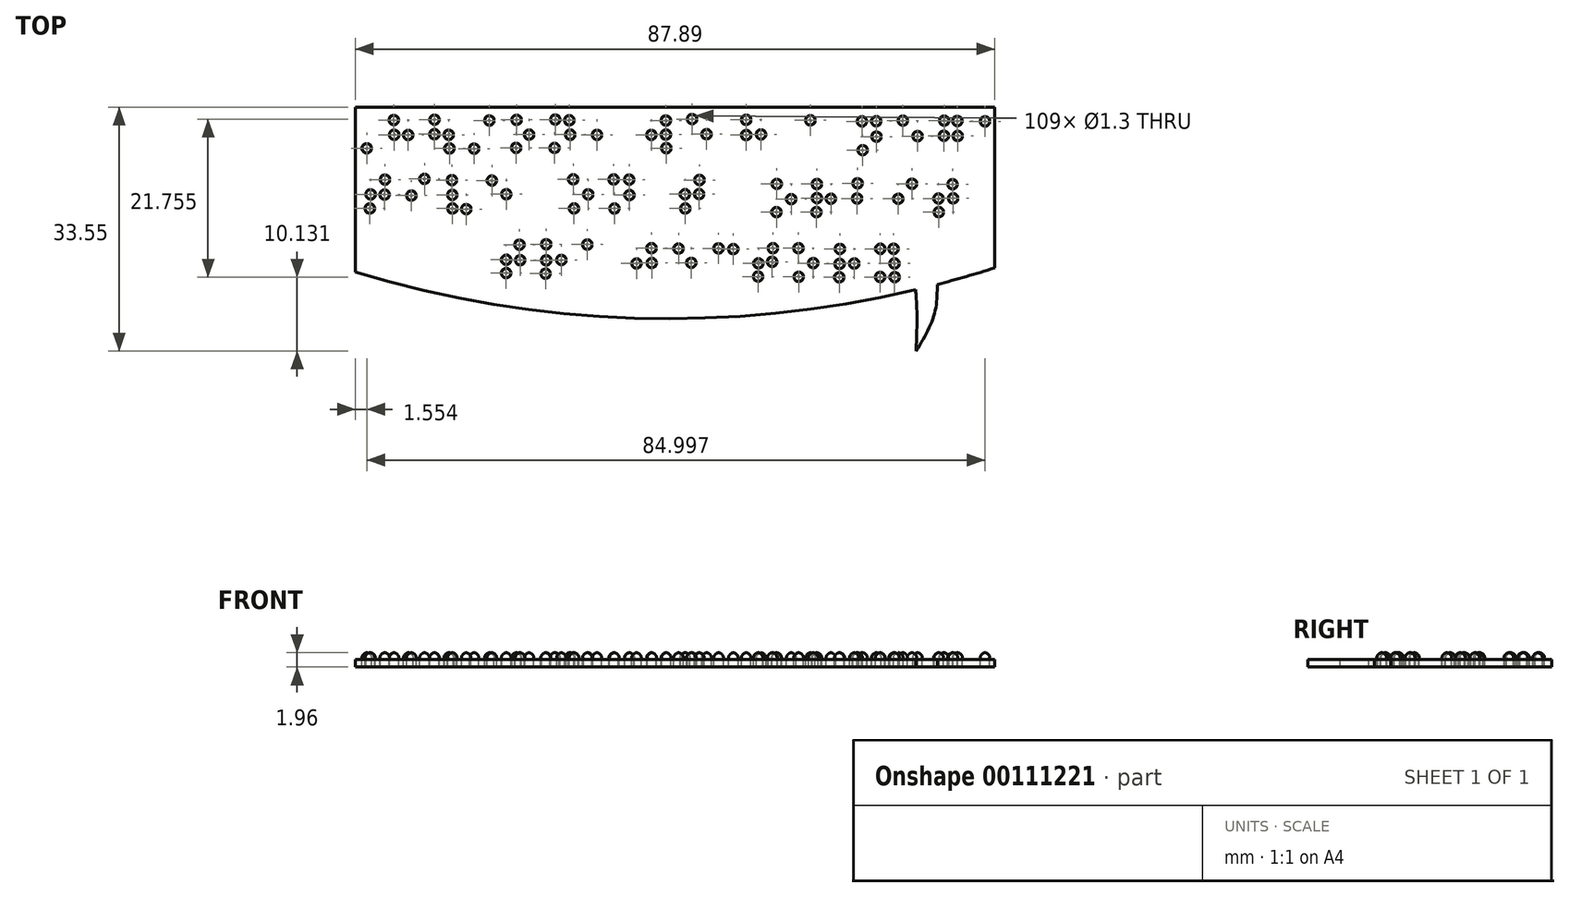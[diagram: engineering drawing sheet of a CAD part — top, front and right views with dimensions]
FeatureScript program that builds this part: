
annotation { "Feature Type Name" : "Feature", "Feature Type Description" : "" }
export const myFeature = defineFeature(function(context is Context, id is Id, definition is map)
    precondition{}
    {
        {
            var Q0;
            Q0=qCreatedBy(makeId("Top.planeOp"),FACE);
            var sketch = newSketch(context, id + "F0", { "sketchPlane" : qUnion([Q0])});
            skCircle(sketch, "E0", {"center": v(-65.84, 32.23) * mm, "radius": 0.65 * mm});
            skSolve(sketch);
        }
        {
            var Q0;
            Q0=qCreatedBy(makeId("Top.planeOp"),FACE);
            var sketch = newSketch(context, id + "F1", { "sketchPlane" : qUnion([Q0])});
            skCircle(sketch, "E1", {"center": v(-52.47, 59.18) * mm, "radius": 0.65 * mm});
            skCircle(sketch, "E2", {"center": v(-52.44, 57.14) * mm, "radius": 0.65 * mm});
            skCircle(sketch, "E3", {"center": v(-50.5, 57.1) * mm, "radius": 0.65 * mm});
            skCircle(sketch, "E4", {"center": v(-56.2, 55.29) * mm, "radius": 0.65 * mm});
            skCircle(sketch, "E5", {"center": v(-46.91, 57.22) * mm, "radius": 0.65 * mm});
            skCircle(sketch, "E6", {"center": v(-46.88, 59.22) * mm, "radius": 0.65 * mm});
            skCircle(sketch, "E7", {"center": v(-44.94, 57.14) * mm, "radius": 0.65 * mm});
            skCircle(sketch, "E8", {"center": v(-44.83, 55.27) * mm, "radius": 0.65 * mm});
            skCircle(sketch, "E9", {"center": v(-41.44, 55.24) * mm, "radius": 0.65 * mm});
            skCircle(sketch, "E10", {"center": v(-39.34, 59.11) * mm, "radius": 0.65 * mm});
            skCircle(sketch, "E11", {"center": v(-35.62, 59.2) * mm, "radius": 0.65 * mm});
            skCircle(sketch, "E12", {"center": v(-33.9, 57.16) * mm, "radius": 0.65 * mm});
            skCircle(sketch, "E13", {"center": v(-35.67, 55.34) * mm, "radius": 0.65 * mm});
            skCircle(sketch, "E14", {"center": v(-30.29, 59.23) * mm, "radius": 0.65 * mm});
            skCircle(sketch, "E15", {"center": v(-28.35, 59.14) * mm, "radius": 0.65 * mm});
            skCircle(sketch, "E16", {"center": v(-28.23, 57.15) * mm, "radius": 0.65 * mm});
            skCircle(sketch, "E17", {"center": v(-30.38, 55.34) * mm, "radius": 0.65 * mm});
            skCircle(sketch, "E18", {"center": v(-24.55, 57.13) * mm, "radius": 0.65 * mm});
            skCircle(sketch, "E19", {"center": v(-17.08, 57.12) * mm, "radius": 0.65 * mm});
            skCircle(sketch, "E20", {"center": v(-15.07, 57.17) * mm, "radius": 0.65 * mm});
            skCircle(sketch, "E21", {"center": v(-15.07, 59.1) * mm, "radius": 0.65 * mm});
            skCircle(sketch, "E22", {"center": v(-15.03, 55.3) * mm, "radius": 0.65 * mm});
            skCircle(sketch, "E23", {"center": v(-11.49, 59.3) * mm, "radius": 0.65 * mm});
            skCircle(sketch, "E24", {"center": v(-9.48, 57.22) * mm, "radius": 0.65 * mm});
            skCircle(sketch, "E25", {"center": v(-4.05, 59.2) * mm, "radius": 0.65 * mm});
            skCircle(sketch, "E26", {"center": v(-4.05, 57.1) * mm, "radius": 0.65 * mm});
            skCircle(sketch, "E27", {"center": v(-2, 57.2) * mm, "radius": 0.65 * mm});
            skCircle(sketch, "E28", {"center": v(4.77, 59.14) * mm, "radius": 0.65 * mm});
            skCircle(sketch, "E29", {"center": v(11.88, 59) * mm, "radius": 0.65 * mm});
            skCircle(sketch, "E30", {"center": v(13.83, 59.02) * mm, "radius": 0.65 * mm});
            skCircle(sketch, "E31", {"center": v(13.86, 56.89) * mm, "radius": 0.65 * mm});
            skCircle(sketch, "E32", {"center": v(11.97, 55.03) * mm, "radius": 0.65 * mm});
            skCircle(sketch, "E33", {"center": v(17.49, 59.09) * mm, "radius": 0.65 * mm});
            skCircle(sketch, "E34", {"center": v(19.52, 56.96) * mm, "radius": 0.65 * mm});
            skCircle(sketch, "E35", {"center": v(23.18, 59.09) * mm, "radius": 0.65 * mm});
            skCircle(sketch, "E36", {"center": v(23.13, 57) * mm, "radius": 0.65 * mm});
            skCircle(sketch, "E37", {"center": v(25.04, 56.98) * mm, "radius": 0.65 * mm});
            skCircle(sketch, "E38", {"center": v(25, 59.04) * mm, "radius": 0.65 * mm});
            skCircle(sketch, "E39", {"center": v(28.8, 58.99) * mm, "radius": 0.65 * mm});
            skCircle(sketch, "E40", {"center": v(-55.68, 48.95) * mm, "radius": 0.65 * mm});
            skCircle(sketch, "E41", {"center": v(-55.77, 47.01) * mm, "radius": 0.65 * mm});
            skCircle(sketch, "E42", {"center": v(-53.74, 48.92) * mm, "radius": 0.65 * mm});
            skCircle(sketch, "E43", {"center": v(-53.7, 50.98) * mm, "radius": 0.65 * mm});
            skCircle(sketch, "E44", {"center": v(-50.06, 48.78) * mm, "radius": 0.65 * mm});
            skCircle(sketch, "E45", {"center": v(-48.27, 51.07) * mm, "radius": 0.65 * mm});
            skCircle(sketch, "E46", {"center": v(-44.5, 50.9) * mm, "radius": 0.65 * mm});
            skCircle(sketch, "E47", {"center": v(-44.45, 48.87) * mm, "radius": 0.65 * mm});
            skCircle(sketch, "E48", {"center": v(-44.43, 47) * mm, "radius": 0.65 * mm});
            skCircle(sketch, "E49", {"center": v(-42.54, 46.91) * mm, "radius": 0.65 * mm});
            skCircle(sketch, "E50", {"center": v(-39, 50.85) * mm, "radius": 0.65 * mm});
            skCircle(sketch, "E51", {"center": v(-37.02, 48.97) * mm, "radius": 0.65 * mm});
            skCircle(sketch, "E52", {"center": v(-27.82, 51.02) * mm, "radius": 0.65 * mm});
            skCircle(sketch, "E53", {"center": v(-25.77, 48.94) * mm, "radius": 0.65 * mm});
            skCircle(sketch, "E54", {"center": v(-27.7, 47) * mm, "radius": 0.65 * mm});
            skCircle(sketch, "E55", {"center": v(-22.25, 51) * mm, "radius": 0.65 * mm});
            skCircle(sketch, "E56", {"center": v(-20.13, 50.97) * mm, "radius": 0.65 * mm});
            skCircle(sketch, "E57", {"center": v(-20.08, 48.84) * mm, "radius": 0.65 * mm});
            skCircle(sketch, "E58", {"center": v(-22.16, 47) * mm, "radius": 0.65 * mm});
            skCircle(sketch, "E59", {"center": v(-12.46, 48.96) * mm, "radius": 0.65 * mm});
            skCircle(sketch, "E60", {"center": v(-12.41, 47) * mm, "radius": 0.65 * mm});
            skCircle(sketch, "E61", {"center": v(-10.52, 48.99) * mm, "radius": 0.65 * mm});
            skCircle(sketch, "E62", {"center": v(-10.47, 50.93) * mm, "radius": 0.65 * mm});
            skCircle(sketch, "E63", {"center": v(0.16, 50.39) * mm, "radius": 0.65 * mm});
            skCircle(sketch, "E64", {"center": v(2.15, 48.3) * mm, "radius": 0.65 * mm});
            skCircle(sketch, "E65", {"center": v(0.12, 46.5) * mm, "radius": 0.65 * mm});
            skCircle(sketch, "E66", {"center": v(5.67, 50.36) * mm, "radius": 0.65 * mm});
            skCircle(sketch, "E67", {"center": v(5.69, 48.42) * mm, "radius": 0.65 * mm});
            skCircle(sketch, "E68", {"center": v(5.62, 46.5) * mm, "radius": 0.65 * mm});
            skCircle(sketch, "E69", {"center": v(7.6, 48.33) * mm, "radius": 0.65 * mm});
            skCircle(sketch, "E70", {"center": v(11.28, 50.48) * mm, "radius": 0.65 * mm});
            skCircle(sketch, "E71", {"center": v(11.2, 48.38) * mm, "radius": 0.65 * mm});
            skCircle(sketch, "E72", {"center": v(16.87, 48.33) * mm, "radius": 0.65 * mm});
            skCircle(sketch, "E73", {"center": v(18.75, 50.4) * mm, "radius": 0.65 * mm});
            skCircle(sketch, "E74", {"center": v(22.4, 48.38) * mm, "radius": 0.65 * mm});
            skCircle(sketch, "E75", {"center": v(24.32, 50.34) * mm, "radius": 0.65 * mm});
            skCircle(sketch, "E76", {"center": v(24.4, 48.4) * mm, "radius": 0.65 * mm});
            skCircle(sketch, "E77", {"center": v(22.44, 46.5) * mm, "radius": 0.65 * mm});
            skCircle(sketch, "E78", {"center": v(-37.03, 38.12) * mm, "radius": 0.65 * mm});
            skCircle(sketch, "E79", {"center": v(-37.03, 39.95) * mm, "radius": 0.65 * mm});
            skCircle(sketch, "E80", {"center": v(-35.12, 39.9) * mm, "radius": 0.65 * mm});
            skCircle(sketch, "E81", {"center": v(-35.2, 42.02) * mm, "radius": 0.65 * mm});
            skCircle(sketch, "E82", {"center": v(-31.53, 42.09) * mm, "radius": 0.65 * mm});
            skCircle(sketch, "E83", {"center": v(-31.53, 39.88) * mm, "radius": 0.65 * mm});
            skCircle(sketch, "E84", {"center": v(-31.62, 38.05) * mm, "radius": 0.65 * mm});
            skCircle(sketch, "E85", {"center": v(-29.46, 39.92) * mm, "radius": 0.65 * mm});
            skCircle(sketch, "E86", {"center": v(-25.9, 42.04) * mm, "radius": 0.65 * mm});
            skCircle(sketch, "E87", {"center": v(-19.12, 39.44) * mm, "radius": 0.65 * mm});
            skCircle(sketch, "E88", {"center": v(-17.02, 39.5) * mm, "radius": 0.65 * mm});
            skCircle(sketch, "E89", {"center": v(-17.07, 41.55) * mm, "radius": 0.65 * mm});
            skCircle(sketch, "E90", {"center": v(-13.34, 41.5) * mm, "radius": 0.65 * mm});
            skCircle(sketch, "E91", {"center": v(-11.59, 39.53) * mm, "radius": 0.65 * mm});
            skCircle(sketch, "E92", {"center": v(-7.83, 41.53) * mm, "radius": 0.65 * mm});
            skCircle(sketch, "E93", {"center": v(-5.8, 41.43) * mm, "radius": 0.65 * mm});
            skCircle(sketch, "E94", {"center": v(-2.36, 39.46) * mm, "radius": 0.65 * mm});
            skCircle(sketch, "E95", {"center": v(-2.41, 37.64) * mm, "radius": 0.65 * mm});
            skCircle(sketch, "E96", {"center": v(-0.47, 39.67) * mm, "radius": 0.65 * mm});
            skCircle(sketch, "E97", {"center": v(-0.38, 41.55) * mm, "radius": 0.65 * mm});
            skCircle(sketch, "E98", {"center": v(3.16, 41.54) * mm, "radius": 0.65 * mm});
            skCircle(sketch, "E99", {"center": v(5.18, 39.5) * mm, "radius": 0.65 * mm});
            skCircle(sketch, "E100", {"center": v(3.17, 37.61) * mm, "radius": 0.65 * mm});
            skCircle(sketch, "E101", {"center": v(8.83, 41.44) * mm, "radius": 0.65 * mm});
            skCircle(sketch, "E102", {"center": v(8.8, 39.39) * mm, "radius": 0.65 * mm});
            skCircle(sketch, "E103", {"center": v(8.75, 37.54) * mm, "radius": 0.65 * mm});
            skCircle(sketch, "E104", {"center": v(10.8, 39.44) * mm, "radius": 0.65 * mm});
            skCircle(sketch, "E105", {"center": v(14.4, 41.46) * mm, "radius": 0.65 * mm});
            skCircle(sketch, "E106", {"center": v(16.22, 41.46) * mm, "radius": 0.65 * mm});
            skCircle(sketch, "E107", {"center": v(16.35, 39.44) * mm, "radius": 0.65 * mm});
            skCircle(sketch, "E108", {"center": v(16.37, 37.57) * mm, "radius": 0.65 * mm});
            skCircle(sketch, "E109", {"center": v(14.37, 37.6) * mm, "radius": 0.65 * mm});
            skLineSegment(sketch, "E110", {"start": v(-57.76, 60.96) * mm, "end": v(30.13, 60.96) * mm});
            skLineSegment(sketch, "E111", {"start": v(30.13, 60.96) * mm, "end": v(30.13, 38.84) * mm});
            skLineSegment(sketch, "E112", {"start": v(-57.76, 60.96) * mm, "end": v(-57.76, 38.27) * mm});
            skArc(sketch, "E113", {"start": v(-57.76, 38.27) * mm, "mid": v(-13.77, 31.86) * mm, "end": v(30.13, 38.84) * mm});
            skFitSpline(sketch, "E114", {"points": [v(22.22, 36.56) * mm, v(21.77, 32.26) * mm, v(19.31, 27.41) * mm], "startDerivative": vector(-0.02, -9.29) * mm, "endDerivative": vector(-5.65, -9.2) * mm});
            skFitSpline(sketch, "E115", {"points": [v(19.25, 35.82) * mm, v(19.43, 32.38) * mm, v(19.31, 27.41) * mm], "startDerivative": vector(0.57, -7.27) * mm, "endDerivative": vector(-0.39, -9.52) * mm});
            skSolve(sketch);
        }
        {
            var Q0;
            Q0=qCreatedBy(makeId("Top.planeOp"),FACE);
            var sketch = newSketch(context, id + "F2", { "sketchPlane" : qUnion([Q0])});
            skLineSegment(sketch, "E116.bottom", {"start": v(-59.53, 60.83) * mm, "end": v(15.65, 60.83) * mm});
            skLineSegment(sketch, "E116.top", {"start": v(-59.53, 26.54) * mm, "end": v(15.65, 26.54) * mm});
            skLineSegment(sketch, "E116.left", {"start": v(-59.53, 60.83) * mm, "end": v(-59.53, 26.54) * mm});
            skLineSegment(sketch, "E116.right", {"start": v(15.65, 60.83) * mm, "end": v(15.65, 26.54) * mm});
            skLineSegment(sketch, "E117.bottom", {"start": v(15.65, 26.54) * mm, "end": v(-12.7, 26.54) * mm});
            skLineSegment(sketch, "E117.top", {"start": v(15.65, 45.59) * mm, "end": v(-12.7, 45.59) * mm});
            skLineSegment(sketch, "E117.left", {"start": v(15.65, 26.54) * mm, "end": v(15.65, 45.59) * mm});
            skLineSegment(sketch, "E117.right", {"start": v(-12.7, 26.54) * mm, "end": v(-12.7, 45.59) * mm});
            skSolve(sketch);
        }
        {
            var Q0;
            Q0=makeQuery(id+"F1.imprint","IMPRINT",FACE,{"disambiguationData":[TD([[makeQuery(id+"F1.imprint","IMPRINT",EDGE,{"derivedFrom":sQuery(id+"F1.wireOp",EDGE,"E81")}),1.0]])]});
            var Q1;
            Q1=makeQuery(id+"F1.imprint","IMPRINT",FACE,{"disambiguationData":[TD([[makeQuery(id+"F1.imprint","IMPRINT",EDGE,{"derivedFrom":sQuery(id+"F1.wireOp",EDGE,"E97")}),1.0]])]});
            var Q2;
            Q2=makeQuery(id+"F1.imprint","IMPRINT",FACE,{"disambiguationData":[TD([[makeQuery(id+"F1.imprint","IMPRINT",EDGE,{"derivedFrom":sQuery(id+"F1.wireOp",EDGE,"E27")}),1.0]])]});
            var Q3;
            Q3=makeQuery(id+"F0.imprint","IMPRINT",FACE,{"disambiguationData":[TD([[makeQuery(id+"F0.imprint","IMPRINT",EDGE,{"derivedFrom":sQuery(id+"F0.wireOp",EDGE,"E0")}),1.0]])]});
            var Q4;
            Q4=makeQuery(id+"F1.imprint","IMPRINT",FACE,{"disambiguationData":[TD([[makeQuery(id+"F1.imprint","IMPRINT",EDGE,{"derivedFrom":sQuery(id+"F1.wireOp",EDGE,"E43")}),1.0]])]});
            var Q5;
            Q5=makeQuery(id+"F1.imprint","IMPRINT",FACE,{"disambiguationData":[TD([[makeQuery(id+"F1.imprint","IMPRINT",EDGE,{"derivedFrom":sQuery(id+"F1.wireOp",EDGE,"E84")}),1.0]])]});
            var Q6;
            Q6=makeQuery(id+"F1.imprint","IMPRINT",FACE,{"disambiguationData":[TD([[makeQuery(id+"F1.imprint","IMPRINT",EDGE,{"derivedFrom":sQuery(id+"F1.wireOp",EDGE,"E100")}),1.0]])]});
            var Q7;
            Q7=makeQuery(id+"F1.imprint","IMPRINT",FACE,{"disambiguationData":[TD([[makeQuery(id+"F1.imprint","IMPRINT",EDGE,{"derivedFrom":sQuery(id+"F1.wireOp",EDGE,"E20")}),1.0]])]});
            var Q8;
            Q8=makeQuery(id+"F1.imprint","IMPRINT",FACE,{"disambiguationData":[TD([[makeQuery(id+"F1.imprint","IMPRINT",EDGE,{"derivedFrom":sQuery(id+"F1.wireOp",EDGE,"E36")}),1.0]])]});
            var Q9;
            Q9=makeQuery(id+"F1.imprint","IMPRINT",FACE,{"disambiguationData":[TD([[makeQuery(id+"F1.imprint","IMPRINT",EDGE,{"derivedFrom":sQuery(id+"F1.wireOp",EDGE,"E58")}),1.0]])]});
            var Q10;
            Q10=makeQuery(id+"F1.imprint","IMPRINT",FACE,{"disambiguationData":[TD([[makeQuery(id+"F1.imprint","IMPRINT",EDGE,{"derivedFrom":sQuery(id+"F1.wireOp",EDGE,"E52")}),1.0]])]});
            var Q11;
            Q11=makeQuery(id+"F1.imprint","IMPRINT",FACE,{"disambiguationData":[TD([[makeQuery(id+"F1.imprint","IMPRINT",EDGE,{"derivedFrom":sQuery(id+"F1.wireOp",EDGE,"E32")}),1.0]])]});
            var Q12;
            Q12=makeQuery(id+"F1.imprint","IMPRINT",FACE,{"disambiguationData":[TD([[makeQuery(id+"F1.imprint","IMPRINT",EDGE,{"derivedFrom":sQuery(id+"F1.wireOp",EDGE,"E74")}),1.0]])]});
            var Q13;
            Q13=makeQuery(id+"F1.imprint","IMPRINT",FACE,{"disambiguationData":[TD([[makeQuery(id+"F1.imprint","IMPRINT",EDGE,{"derivedFrom":sQuery(id+"F1.wireOp",EDGE,"E48")}),1.0]])]});
            var Q14;
            Q14=makeQuery(id+"F1.imprint","IMPRINT",FACE,{"disambiguationData":[TD([[makeQuery(id+"F1.imprint","IMPRINT",EDGE,{"derivedFrom":sQuery(id+"F1.wireOp",EDGE,"E90")}),1.0]])]});
            var Q15;
            Q15=makeQuery(id+"F1.imprint","IMPRINT",FACE,{"disambiguationData":[TD([[makeQuery(id+"F1.imprint","IMPRINT",EDGE,{"derivedFrom":sQuery(id+"F1.wireOp",EDGE,"E64")}),1.0]])]});
            var Q16;
            Q16=makeQuery(id+"F1.imprint","IMPRINT",FACE,{"disambiguationData":[TD([[makeQuery(id+"F1.imprint","IMPRINT",EDGE,{"derivedFrom":sQuery(id+"F1.wireOp",EDGE,"E80")}),1.0]])]});
            var Q17;
            Q17=makeQuery(id+"F1.imprint","IMPRINT",FACE,{"disambiguationData":[TD([[makeQuery(id+"F1.imprint","IMPRINT",EDGE,{"derivedFrom":sQuery(id+"F1.wireOp",EDGE,"E106")}),1.0]])]});
            var Q18;
            Q18=makeQuery(id+"F1.imprint","IMPRINT",FACE,{"disambiguationData":[TD([[makeQuery(id+"F1.imprint","IMPRINT",EDGE,{"derivedFrom":sQuery(id+"F1.wireOp",EDGE,"E26")}),1.0]])]});
            var Q19;
            Q19=makeQuery(id+"F1.imprint","IMPRINT",FACE,{"disambiguationData":[TD([[makeQuery(id+"F1.imprint","IMPRINT",EDGE,{"derivedFrom":sQuery(id+"F1.wireOp",EDGE,"E42")}),1.0]])]});
            var Q20;
            Q20=makeQuery(id+"F1.imprint","IMPRINT",FACE,{"disambiguationData":[TD([[makeQuery(id+"F1.imprint","IMPRINT",EDGE,{"derivedFrom":sQuery(id+"F1.wireOp",EDGE,"E83")}),1.0]])]});
            var Q21;
            Q21=makeQuery(id+"F1.imprint","IMPRINT",FACE,{"disambiguationData":[TD([[makeQuery(id+"F1.imprint","IMPRINT",EDGE,{"derivedFrom":sQuery(id+"F1.wireOp",EDGE,"E99")}),1.0]])]});
            var Q22;
            Q22=makeQuery(id+"F1.imprint","IMPRINT",FACE,{"disambiguationData":[TD([[makeQuery(id+"F1.imprint","IMPRINT",EDGE,{"derivedFrom":sQuery(id+"F1.wireOp",EDGE,"E17")}),1.0]])]});
            var Q23;
            Q23=makeQuery(id+"F1.imprint","IMPRINT",FACE,{"disambiguationData":[TD([[makeQuery(id+"F1.imprint","IMPRINT",EDGE,{"derivedFrom":sQuery(id+"F1.wireOp",EDGE,"E33")}),1.0]])]});
            var Q24;
            Q24=makeQuery(id+"F1.imprint","IMPRINT",FACE,{"disambiguationData":[TD([[makeQuery(id+"F1.imprint","IMPRINT",EDGE,{"derivedFrom":sQuery(id+"F1.wireOp",EDGE,"E23")}),1.0]])]});
            var Q25;
            Q25=makeQuery(id+"F1.imprint","IMPRINT",FACE,{"disambiguationData":[TD([[makeQuery(id+"F1.imprint","IMPRINT",EDGE,{"derivedFrom":sQuery(id+"F1.wireOp",EDGE,"E39")}),1.0]])]});
            var Q26;
            Q26=makeQuery(id+"F1.imprint","IMPRINT",FACE,{"disambiguationData":[TD([[makeQuery(id+"F1.imprint","IMPRINT",EDGE,{"derivedFrom":sQuery(id+"F1.wireOp",EDGE,"E55")}),1.0]])]});
            var Q27;
            Q27=makeQuery(id+"F1.imprint","IMPRINT",FACE,{"disambiguationData":[TD([[makeQuery(id+"F1.imprint","IMPRINT",EDGE,{"derivedFrom":sQuery(id+"F1.wireOp",EDGE,"E71")}),1.0]])]});
            var Q28;
            Q28=makeQuery(id+"F1.imprint","IMPRINT",FACE,{"disambiguationData":[TD([[makeQuery(id+"F1.imprint","IMPRINT",EDGE,{"derivedFrom":sQuery(id+"F1.wireOp",EDGE,"E87")}),1.0]])]});
            var Q29;
            Q29=makeQuery(id+"F1.imprint","IMPRINT",FACE,{"disambiguationData":[TD([[makeQuery(id+"F1.imprint","IMPRINT",EDGE,{"derivedFrom":sQuery(id+"F1.wireOp",EDGE,"E49")}),1.0]])]});
            var Q30;
            Q30=makeQuery(id+"F1.imprint","IMPRINT",FACE,{"disambiguationData":[TD([[makeQuery(id+"F1.imprint","IMPRINT",EDGE,{"derivedFrom":sQuery(id+"F1.wireOp",EDGE,"E65")}),1.0]])]});
            var Q31;
            Q31=makeQuery(id+"F1.imprint","IMPRINT",FACE,{"disambiguationData":[TD([[makeQuery(id+"F1.imprint","IMPRINT",EDGE,{"derivedFrom":sQuery(id+"F1.wireOp",EDGE,"E19")}),1.0]])]});
            var Q32;
            Q32=makeQuery(id+"F1.imprint","IMPRINT",FACE,{"disambiguationData":[TD([[makeQuery(id+"F1.imprint","IMPRINT",EDGE,{"derivedFrom":sQuery(id+"F1.wireOp",EDGE,"E51")}),1.0]])]});
            var Q33;
            Q33=makeQuery(id+"F1.imprint","IMPRINT",FACE,{"disambiguationData":[TD([[makeQuery(id+"F1.imprint","IMPRINT",EDGE,{"derivedFrom":sQuery(id+"F1.wireOp",EDGE,"E57")}),1.0]])]});
            var Q34;
            Q34=makeQuery(id+"F1.imprint","IMPRINT",FACE,{"disambiguationData":[TD([[makeQuery(id+"F1.imprint","IMPRINT",EDGE,{"derivedFrom":sQuery(id+"F1.wireOp",EDGE,"E73")}),1.0]])]});
            var Q35;
            Q35=makeQuery(id+"F1.imprint","IMPRINT",FACE,{"disambiguationData":[TD([[makeQuery(id+"F1.imprint","IMPRINT",EDGE,{"derivedFrom":sQuery(id+"F1.wireOp",EDGE,"E89")}),1.0]])]});
            var Q36;
            Q36=makeQuery(id+"F1.imprint","IMPRINT",FACE,{"disambiguationData":[TD([[makeQuery(id+"F1.imprint","IMPRINT",EDGE,{"derivedFrom":sQuery(id+"F1.wireOp",EDGE,"E105")}),1.0]])]});
            var Q37;
            Q37=makeQuery(id+"F1.imprint","IMPRINT",FACE,{"disambiguationData":[TD([[makeQuery(id+"F1.imprint","IMPRINT",EDGE,{"derivedFrom":sQuery(id+"F1.wireOp",EDGE,"E61")}),1.0]])]});
            var Q38;
            Q38=makeQuery(id+"F1.imprint","IMPRINT",FACE,{"disambiguationData":[TD([[makeQuery(id+"F1.imprint","IMPRINT",EDGE,{"derivedFrom":sQuery(id+"F1.wireOp",EDGE,"E77")}),1.0]])]});
            var Q39;
            Q39=makeQuery(id+"F1.imprint","IMPRINT",FACE,{"disambiguationData":[TD([[makeQuery(id+"F1.imprint","IMPRINT",EDGE,{"derivedFrom":sQuery(id+"F1.wireOp",EDGE,"E13")}),1.0]])]});
            var Q40;
            Q40=makeQuery(id+"F1.imprint","IMPRINT",FACE,{"disambiguationData":[TD([[makeQuery(id+"F1.imprint","IMPRINT",EDGE,{"derivedFrom":sQuery(id+"F1.wireOp",EDGE,"E10")}),1.0]])]});
            var Q41;
            Q41=makeQuery(id+"F1.imprint","IMPRINT",FACE,{"disambiguationData":[TD([[makeQuery(id+"F1.imprint","IMPRINT",EDGE,{"derivedFrom":sQuery(id+"F1.wireOp",EDGE,"E12")}),1.0]])]});
            var Q42;
            Q42=makeQuery(id+"F1.imprint","IMPRINT",FACE,{"disambiguationData":[TD([[makeQuery(id+"F1.imprint","IMPRINT",EDGE,{"derivedFrom":sQuery(id+"F1.wireOp",EDGE,"E11")}),1.0]])]});
            var Q43;
            Q43=makeQuery(id+"F1.imprint","IMPRINT",FACE,{"disambiguationData":[TD([[makeQuery(id+"F1.imprint","IMPRINT",EDGE,{"derivedFrom":sQuery(id+"F1.wireOp",EDGE,"E25")}),1.0]])]});
            var Q44;
            Q44=makeQuery(id+"F1.imprint","IMPRINT",FACE,{"disambiguationData":[TD([[makeQuery(id+"F1.imprint","IMPRINT",EDGE,{"derivedFrom":sQuery(id+"F1.wireOp",EDGE,"E7")}),1.0]])]});
            var Q45;
            Q45=makeQuery(id+"F1.imprint","IMPRINT",FACE,{"disambiguationData":[TD([[makeQuery(id+"F1.imprint","IMPRINT",EDGE,{"derivedFrom":sQuery(id+"F1.wireOp",EDGE,"E8")}),1.0]])]});
            var Q46;
            Q46=makeQuery(id+"F1.imprint","IMPRINT",FACE,{"disambiguationData":[TD([[makeQuery(id+"F1.imprint","IMPRINT",EDGE,{"derivedFrom":sQuery(id+"F1.wireOp",EDGE,"E41")}),1.0]])]});
            var Q47;
            Q47=makeQuery(id+"F1.imprint","IMPRINT",FACE,{"disambiguationData":[TD([[makeQuery(id+"F1.imprint","IMPRINT",EDGE,{"derivedFrom":sQuery(id+"F1.wireOp",EDGE,"E82")}),1.0]])]});
            var Q48;
            Q48=makeQuery(id+"F1.imprint","IMPRINT",FACE,{"disambiguationData":[TD([[makeQuery(id+"F1.imprint","IMPRINT",EDGE,{"derivedFrom":sQuery(id+"F1.wireOp",EDGE,"E93")}),1.0]])]});
            var Q49;
            Q49=makeQuery(id+"F1.imprint","IMPRINT",FACE,{"disambiguationData":[TD([[makeQuery(id+"F1.imprint","IMPRINT",EDGE,{"derivedFrom":sQuery(id+"F1.wireOp",EDGE,"E98")}),1.0]])]});
            var Q50;
            Q50=makeQuery(id+"F1.imprint","IMPRINT",FACE,{"disambiguationData":[TD([[makeQuery(id+"F1.imprint","IMPRINT",EDGE,{"derivedFrom":sQuery(id+"F1.wireOp",EDGE,"E18")}),1.0]])]});
            var Q51;
            Q51=makeQuery(id+"F1.imprint","IMPRINT",FACE,{"disambiguationData":[TD([[makeQuery(id+"F1.imprint","IMPRINT",EDGE,{"derivedFrom":sQuery(id+"F1.wireOp",EDGE,"E34")}),1.0]])]});
            var Q52;
            Q52=makeQuery(id+"F1.imprint","IMPRINT",FACE,{"disambiguationData":[TD([[makeQuery(id+"F1.imprint","IMPRINT",EDGE,{"derivedFrom":sQuery(id+"F1.wireOp",EDGE,"E50")}),1.0]])]});
            var Q53;
            Q53=makeQuery(id+"F1.imprint","IMPRINT",FACE,{"disambiguationData":[TD([[makeQuery(id+"F1.imprint","IMPRINT",EDGE,{"derivedFrom":sQuery(id+"F1.wireOp",EDGE,"E45")}),1.0]])]});
            var Q54;
            Q54=makeQuery(id+"F1.imprint","IMPRINT",FACE,{"disambiguationData":[TD([[makeQuery(id+"F1.imprint","IMPRINT",EDGE,{"derivedFrom":sQuery(id+"F1.wireOp",EDGE,"E86")}),1.0]])]});
            var Q55;
            Q55=makeQuery(id+"F1.imprint","IMPRINT",FACE,{"disambiguationData":[TD([[makeQuery(id+"F1.imprint","IMPRINT",EDGE,{"derivedFrom":sQuery(id+"F1.wireOp",EDGE,"E79")}),1.0]])]});
            var Q56;
            Q56=makeQuery(id+"F1.imprint","IMPRINT",FACE,{"disambiguationData":[TD([[makeQuery(id+"F1.imprint","IMPRINT",EDGE,{"derivedFrom":sQuery(id+"F1.wireOp",EDGE,"E31")}),1.0]])]});
            var Q57;
            Q57=makeQuery(id+"F1.imprint","IMPRINT",FACE,{"disambiguationData":[TD([[makeQuery(id+"F1.imprint","IMPRINT",EDGE,{"derivedFrom":sQuery(id+"F1.wireOp",EDGE,"E22")}),1.0]])]});
            var Q58;
            Q58=makeQuery(id+"F1.imprint","IMPRINT",FACE,{"disambiguationData":[TD([[makeQuery(id+"F1.imprint","IMPRINT",EDGE,{"derivedFrom":sQuery(id+"F1.wireOp",EDGE,"E54")}),1.0]])]});
            var Q59;
            Q59=makeQuery(id+"F1.imprint","IMPRINT",FACE,{"disambiguationData":[TD([[makeQuery(id+"F1.imprint","IMPRINT",EDGE,{"derivedFrom":sQuery(id+"F1.wireOp",EDGE,"E6")}),1.0]])]});
            var Q60;
            Q60=makeQuery(id+"F1.imprint","IMPRINT",FACE,{"disambiguationData":[TD([[makeQuery(id+"F1.imprint","IMPRINT",EDGE,{"derivedFrom":sQuery(id+"F1.wireOp",EDGE,"E66")}),1.0]])]});
            var Q61;
            Q61=makeQuery(id+"F1.imprint","IMPRINT",FACE,{"disambiguationData":[TD([[makeQuery(id+"F1.imprint","IMPRINT",EDGE,{"derivedFrom":sQuery(id+"F1.wireOp",EDGE,"E5")}),1.0]])]});
            var Q62;
            Q62=makeQuery(id+"F1.imprint","IMPRINT",FACE,{"disambiguationData":[TD([[makeQuery(id+"F1.imprint","IMPRINT",EDGE,{"derivedFrom":sQuery(id+"F1.wireOp",EDGE,"E70")}),1.0]])]});
            var Q63;
            Q63=makeQuery(id+"F1.imprint","IMPRINT",FACE,{"disambiguationData":[TD([[makeQuery(id+"F1.imprint","IMPRINT",EDGE,{"derivedFrom":sQuery(id+"F1.wireOp",EDGE,"E47")}),1.0]])]});
            var Q64;
            Q64=makeQuery(id+"F1.imprint","IMPRINT",FACE,{"disambiguationData":[TD([[makeQuery(id+"F1.imprint","IMPRINT",EDGE,{"derivedFrom":sQuery(id+"F1.wireOp",EDGE,"E63")}),1.0]])]});
            var Q65;
            Q65=makeQuery(id+"F1.imprint","IMPRINT",FACE,{"disambiguationData":[TD([[makeQuery(id+"F1.imprint","IMPRINT",EDGE,{"derivedFrom":sQuery(id+"F1.wireOp",EDGE,"E4")}),1.0]])]});
            var Q66;
            Q66=makeQuery(id+"F1.imprint","IMPRINT",FACE,{"disambiguationData":[TD([[makeQuery(id+"F1.imprint","IMPRINT",EDGE,{"derivedFrom":sQuery(id+"F1.wireOp",EDGE,"E3")}),1.0]])]});
            var Q67;
            Q67=makeQuery(id+"F1.imprint","IMPRINT",FACE,{"disambiguationData":[TD([[makeQuery(id+"F1.imprint","IMPRINT",EDGE,{"derivedFrom":sQuery(id+"F1.wireOp",EDGE,"E2")}),1.0]])]});
            var Q68;
            Q68=makeQuery(id+"F1.imprint","IMPRINT",FACE,{"disambiguationData":[TD([[makeQuery(id+"F1.imprint","IMPRINT",EDGE,{"derivedFrom":sQuery(id+"F1.wireOp",EDGE,"E56")}),1.0]])]});
            var Q69;
            Q69=makeQuery(id+"F1.imprint","IMPRINT",FACE,{"disambiguationData":[TD([[makeQuery(id+"F1.imprint","IMPRINT",EDGE,{"derivedFrom":sQuery(id+"F1.wireOp",EDGE,"E72")}),1.0]])]});
            var Q70;
            Q70=makeQuery(id+"F1.imprint","IMPRINT",FACE,{"disambiguationData":[TD([[makeQuery(id+"F1.imprint","IMPRINT",EDGE,{"derivedFrom":sQuery(id+"F1.wireOp",EDGE,"E1")}),1.0]])]});
            var Q71;
            Q71=makeQuery(id+"F1.imprint","IMPRINT",FACE,{"disambiguationData":[TD([[makeQuery(id+"F1.imprint","IMPRINT",EDGE,{"derivedFrom":sQuery(id+"F1.wireOp",EDGE,"E88")}),1.0]])]});
            var Q72;
            Q72=makeQuery(id+"F1.imprint","IMPRINT",FACE,{"disambiguationData":[TD([[makeQuery(id+"F1.imprint","IMPRINT",EDGE,{"derivedFrom":sQuery(id+"F1.wireOp",EDGE,"E60")}),1.0]])]});
            var Q73;
            Q73=makeQuery(id+"F1.imprint","IMPRINT",FACE,{"disambiguationData":[TD([[makeQuery(id+"F1.imprint","IMPRINT",EDGE,{"derivedFrom":sQuery(id+"F1.wireOp",EDGE,"E76")}),1.0]])]});
            var Q74;
            Q74=makeQuery(id+"F1.imprint","IMPRINT",FACE,{"disambiguationData":[TD([[makeQuery(id+"F1.imprint","IMPRINT",EDGE,{"derivedFrom":sQuery(id+"F1.wireOp",EDGE,"E92")}),1.0]])]});
            var Q75;
            Q75=makeQuery(id+"F1.imprint","IMPRINT",FACE,{"disambiguationData":[TD([[makeQuery(id+"F1.imprint","IMPRINT",EDGE,{"derivedFrom":sQuery(id+"F1.wireOp",EDGE,"E15")}),1.0]])]});
            var Q76;
            Q76=makeQuery(id+"F1.imprint","IMPRINT",FACE,{"disambiguationData":[TD([[makeQuery(id+"F1.imprint","IMPRINT",EDGE,{"derivedFrom":sQuery(id+"F1.wireOp",EDGE,"E14")}),1.0]])]});
            var Q77;
            Q77=makeQuery(id+"F1.imprint","IMPRINT",FACE,{"disambiguationData":[TD([[makeQuery(id+"F1.imprint","IMPRINT",EDGE,{"derivedFrom":sQuery(id+"F1.wireOp",EDGE,"E44")}),1.0]])]});
            var Q78;
            Q78=makeQuery(id+"F1.imprint","IMPRINT",FACE,{"disambiguationData":[TD([[makeQuery(id+"F1.imprint","IMPRINT",EDGE,{"derivedFrom":sQuery(id+"F1.wireOp",EDGE,"E28")}),1.0]])]});
            var Q79;
            Q79=makeQuery(id+"F1.imprint","IMPRINT",FACE,{"disambiguationData":[TD([[makeQuery(id+"F1.imprint","IMPRINT",EDGE,{"derivedFrom":sQuery(id+"F1.wireOp",EDGE,"E78")}),1.0]])]});
            var Q80;
            Q80=makeQuery(id+"F1.imprint","IMPRINT",FACE,{"disambiguationData":[TD([[makeQuery(id+"F1.imprint","IMPRINT",EDGE,{"derivedFrom":sQuery(id+"F1.wireOp",EDGE,"E85")}),1.0]])]});
            var Q81;
            Q81=makeQuery(id+"F1.imprint","IMPRINT",FACE,{"disambiguationData":[TD([[makeQuery(id+"F1.imprint","IMPRINT",EDGE,{"derivedFrom":sQuery(id+"F1.wireOp",EDGE,"E16")}),1.0]])]});
            var Q82;
            Q82=makeQuery(id+"F1.imprint","IMPRINT",FACE,{"disambiguationData":[TD([[makeQuery(id+"F1.imprint","IMPRINT",EDGE,{"derivedFrom":sQuery(id+"F1.wireOp",EDGE,"E24")}),1.0]])]});
            var Q83;
            Q83=makeQuery(id+"F1.imprint","IMPRINT",FACE,{"disambiguationData":[TD([[makeQuery(id+"F1.imprint","IMPRINT",EDGE,{"derivedFrom":sQuery(id+"F1.wireOp",EDGE,"E40")}),1.0]])]});
            var Q84;
            Q84=makeQuery(id+"F1.imprint","IMPRINT",FACE,{"disambiguationData":[TD([[makeQuery(id+"F1.imprint","IMPRINT",EDGE,{"derivedFrom":sQuery(id+"F1.wireOp",EDGE,"E101")}),1.0]])]});
            var Q85;
            Q85=makeQuery(id+"F1.imprint","IMPRINT",FACE,{"disambiguationData":[TD([[makeQuery(id+"F1.imprint","IMPRINT",EDGE,{"derivedFrom":sQuery(id+"F1.wireOp",EDGE,"E21")}),1.0]])]});
            var Q86;
            Q86=makeQuery(id+"F1.imprint","IMPRINT",FACE,{"disambiguationData":[TD([[makeQuery(id+"F1.imprint","IMPRINT",EDGE,{"derivedFrom":sQuery(id+"F1.wireOp",EDGE,"E37")}),1.0]])]});
            var Q87;
            Q87=makeQuery(id+"F1.imprint","IMPRINT",FACE,{"disambiguationData":[TD([[makeQuery(id+"F1.imprint","IMPRINT",EDGE,{"derivedFrom":sQuery(id+"F1.wireOp",EDGE,"E46")}),1.0]])]});
            var Q88;
            Q88=makeQuery(id+"F1.imprint","IMPRINT",FACE,{"disambiguationData":[TD([[makeQuery(id+"F1.imprint","IMPRINT",EDGE,{"derivedFrom":sQuery(id+"F1.wireOp",EDGE,"E62")}),1.0]])]});
            var Q89;
            Q89=makeQuery(id+"F1.imprint","IMPRINT",FACE,{"disambiguationData":[TD([[makeQuery(id+"F1.imprint","IMPRINT",EDGE,{"derivedFrom":sQuery(id+"F1.wireOp",EDGE,"E59")}),1.0]])]});
            var Q90;
            Q90=makeQuery(id+"F1.imprint","IMPRINT",FACE,{"disambiguationData":[TD([[makeQuery(id+"F1.imprint","IMPRINT",EDGE,{"derivedFrom":sQuery(id+"F1.wireOp",EDGE,"E75")}),1.0]])]});
            var Q91;
            Q91=makeQuery(id+"F1.imprint","IMPRINT",FACE,{"disambiguationData":[TD([[makeQuery(id+"F1.imprint","IMPRINT",EDGE,{"derivedFrom":sQuery(id+"F1.wireOp",EDGE,"E91")}),1.0]])]});
            var Q92;
            Q92=makeQuery(id+"F1.imprint","IMPRINT",FACE,{"disambiguationData":[TD([[makeQuery(id+"F1.imprint","IMPRINT",EDGE,{"derivedFrom":sQuery(id+"F1.wireOp",EDGE,"E9")}),1.0]])]});
            var Q93;
            Q93=makeQuery(id+"F1.imprint","IMPRINT",FACE,{"disambiguationData":[TD([[makeQuery(id+"F1.imprint","IMPRINT",EDGE,{"derivedFrom":sQuery(id+"F1.wireOp",EDGE,"E96")}),1.0]])]});
            var Q94;
            Q94=makeQuery(id+"F1.imprint","IMPRINT",FACE,{"disambiguationData":[TD([[makeQuery(id+"F1.imprint","IMPRINT",EDGE,{"derivedFrom":sQuery(id+"F1.wireOp",EDGE,"E68")}),1.0]])]});
            var Q95;
            Q95=makeQuery(id+"F1.imprint","IMPRINT",FACE,{"disambiguationData":[TD([[makeQuery(id+"F1.imprint","IMPRINT",EDGE,{"derivedFrom":sQuery(id+"F1.wireOp",EDGE,"E35")}),1.0]])]});
            var Q96;
            Q96=makeQuery(id+"F1.imprint","IMPRINT",FACE,{"disambiguationData":[TD([[makeQuery(id+"F1.imprint","IMPRINT",EDGE,{"derivedFrom":sQuery(id+"F1.wireOp",EDGE,"E103")}),1.0]])]});
            var Q97;
            Q97=makeQuery(id+"F1.imprint","IMPRINT",FACE,{"disambiguationData":[TD([[makeQuery(id+"F1.imprint","IMPRINT",EDGE,{"derivedFrom":sQuery(id+"F1.wireOp",EDGE,"E67")}),1.0]])]});
            var Q98;
            Q98=makeQuery(id+"F1.imprint","IMPRINT",FACE,{"disambiguationData":[TD([[makeQuery(id+"F1.imprint","IMPRINT",EDGE,{"derivedFrom":sQuery(id+"F1.wireOp",EDGE,"E109")}),1.0]])]});
            var Q99;
            Q99=makeQuery(id+"F1.imprint","IMPRINT",FACE,{"disambiguationData":[TD([[makeQuery(id+"F1.imprint","IMPRINT",EDGE,{"derivedFrom":sQuery(id+"F1.wireOp",EDGE,"E29")}),1.0]])]});
            var Q100;
            Q100=makeQuery(id+"F1.imprint","IMPRINT",FACE,{"disambiguationData":[TD([[makeQuery(id+"F1.imprint","IMPRINT",EDGE,{"derivedFrom":sQuery(id+"F1.wireOp",EDGE,"E102")}),1.0]])]});
            var Q101;
            Q101=makeQuery(id+"F1.imprint","IMPRINT",FACE,{"disambiguationData":[TD([[makeQuery(id+"F1.imprint","IMPRINT",EDGE,{"derivedFrom":sQuery(id+"F1.wireOp",EDGE,"E95")}),1.0]])]});
            var Q102;
            Q102=makeQuery(id+"F1.imprint","IMPRINT",FACE,{"disambiguationData":[TD([[makeQuery(id+"F1.imprint","IMPRINT",EDGE,{"derivedFrom":sQuery(id+"F1.wireOp",EDGE,"E38")}),1.0]])]});
            var Q103;
            Q103=makeQuery(id+"F1.imprint","IMPRINT",FACE,{"disambiguationData":[TD([[makeQuery(id+"F1.imprint","IMPRINT",EDGE,{"derivedFrom":sQuery(id+"F1.wireOp",EDGE,"E108")}),1.0]])]});
            var Q104;
            Q104=makeQuery(id+"F1.imprint","IMPRINT",FACE,{"disambiguationData":[TD([[makeQuery(id+"F1.imprint","IMPRINT",EDGE,{"derivedFrom":sQuery(id+"F1.wireOp",EDGE,"E104")}),1.0]])]});
            var Q105;
            Q105=makeQuery(id+"F1.imprint","IMPRINT",FACE,{"disambiguationData":[TD([[makeQuery(id+"F1.imprint","IMPRINT",EDGE,{"derivedFrom":sQuery(id+"F1.wireOp",EDGE,"E94")}),1.0]])]});
            var Q106;
            Q106=makeQuery(id+"F1.imprint","IMPRINT",FACE,{"disambiguationData":[TD([[makeQuery(id+"F1.imprint","IMPRINT",EDGE,{"derivedFrom":sQuery(id+"F1.wireOp",EDGE,"E30")}),1.0]])]});
            var Q107;
            Q107=makeQuery(id+"F1.imprint","IMPRINT",FACE,{"disambiguationData":[TD([[makeQuery(id+"F1.imprint","IMPRINT",EDGE,{"derivedFrom":sQuery(id+"F1.wireOp",EDGE,"E53")}),1.0]])]});
            var Q108;
            Q108=makeQuery(id+"F1.imprint","IMPRINT",FACE,{"disambiguationData":[TD([[makeQuery(id+"F1.imprint","IMPRINT",EDGE,{"derivedFrom":sQuery(id+"F1.wireOp",EDGE,"E69")}),1.0]])]});
            var Q109;
            Q109=makeQuery(id+"F1.imprint","IMPRINT",FACE,{"disambiguationData":[TD([[makeQuery(id+"F1.imprint","IMPRINT",EDGE,{"derivedFrom":sQuery(id+"F1.wireOp",EDGE,"E107")}),1.0]])]});
            extrude(context, id + "F3", {"entities" : qUnion([Q0, Q1, Q2, Q3, Q4, Q5, Q6, Q7, Q8, Q9, Q10, Q11, Q12, Q13, Q14, Q15, Q16, Q17, Q18, Q19, Q20, Q21, Q22, Q23, Q24, Q25, Q26, Q27, Q28, Q29, Q30, Q31, Q32, Q33, Q34, Q35, Q36, Q37, Q38, Q39, Q40, Q41, Q42, Q43, Q44, Q45, Q46, Q47, Q48, Q49, Q50, Q51, Q52, Q53, Q54, Q55, Q56, Q57, Q58, Q59, Q60, Q61, Q62, Q63, Q64, Q65, Q66, Q67, Q68, Q69, Q70, Q71, Q72, Q73, Q74, Q75, Q76, Q77, Q78, Q79, Q80, Q81, Q82, Q83, Q84, Q85, Q86, Q87, Q88, Q89, Q90, Q91, Q92, Q93, Q94, Q95, Q96, Q97, Q98, Q99, Q100, Q101, Q102, Q103, Q104, Q105, Q106, Q107, Q108, Q109]), "depth" : 0.94 * mm});
        }
        {
            var Q0;
            Q0=makeQuery(id+"F3.opExtrude","CAP_EDGE",EDGE,{"disambiguationData":[OSD([sQuery(id+"F1.wireOp",EDGE,"E4")])],"isStart":false});
            var Q1;
            Q1=makeQuery(id+"F3.opExtrude","CAP_EDGE",EDGE,{"disambiguationData":[OSD([sQuery(id+"F1.wireOp",EDGE,"E2")])],"isStart":false});
            var Q2;
            Q2=makeQuery(id+"F3.opExtrude","CAP_EDGE",EDGE,{"disambiguationData":[OSD([sQuery(id+"F1.wireOp",EDGE,"E3")])],"isStart":false});
            var Q3;
            Q3=makeQuery(id+"F3.opExtrude","CAP_EDGE",EDGE,{"disambiguationData":[OSD([sQuery(id+"F1.wireOp",EDGE,"E5")])],"isStart":false});
            var Q4;
            Q4=makeQuery(id+"F3.opExtrude","CAP_EDGE",EDGE,{"disambiguationData":[OSD([sQuery(id+"F1.wireOp",EDGE,"E8")])],"isStart":false});
            var Q5;
            Q5=makeQuery(id+"F3.opExtrude","CAP_EDGE",EDGE,{"disambiguationData":[OSD([sQuery(id+"F1.wireOp",EDGE,"E9")])],"isStart":false});
            var Q6;
            Q6=makeQuery(id+"F3.opExtrude","CAP_EDGE",EDGE,{"disambiguationData":[OSD([sQuery(id+"F1.wireOp",EDGE,"E15")])],"isStart":false});
            var Q7;
            Q7=makeQuery(id+"F3.opExtrude","CAP_EDGE",EDGE,{"disambiguationData":[OSD([sQuery(id+"F1.wireOp",EDGE,"E14")])],"isStart":false});
            var Q8;
            Q8=makeQuery(id+"F3.opExtrude","CAP_EDGE",EDGE,{"disambiguationData":[OSD([sQuery(id+"F1.wireOp",EDGE,"E16")])],"isStart":false});
            var Q9;
            Q9=makeQuery(id+"F3.opExtrude","CAP_EDGE",EDGE,{"disambiguationData":[OSD([sQuery(id+"F1.wireOp",EDGE,"E18")])],"isStart":false});
            var Q10;
            Q10=makeQuery(id+"F3.opExtrude","CAP_EDGE",EDGE,{"disambiguationData":[OSD([sQuery(id+"F1.wireOp",EDGE,"E17")])],"isStart":false});
            var Q11;
            Q11=makeQuery(id+"F3.opExtrude","CAP_EDGE",EDGE,{"disambiguationData":[OSD([sQuery(id+"F1.wireOp",EDGE,"E12")])],"isStart":false});
            var Q12;
            Q12=makeQuery(id+"F3.opExtrude","CAP_EDGE",EDGE,{"disambiguationData":[OSD([sQuery(id+"F1.wireOp",EDGE,"E13")])],"isStart":false});
            var Q13;
            Q13=makeQuery(id+"F3.opExtrude","CAP_EDGE",EDGE,{"disambiguationData":[OSD([sQuery(id+"F1.wireOp",EDGE,"E7")])],"isStart":false});
            var Q14;
            Q14=makeQuery(id+"F3.opExtrude","CAP_EDGE",EDGE,{"disambiguationData":[OSD([sQuery(id+"F1.wireOp",EDGE,"E10")])],"isStart":false});
            var Q15;
            Q15=makeQuery(id+"F3.opExtrude","CAP_EDGE",EDGE,{"disambiguationData":[OSD([sQuery(id+"F1.wireOp",EDGE,"E11")])],"isStart":false});
            var Q16;
            Q16=makeQuery(id+"F3.opExtrude","CAP_EDGE",EDGE,{"disambiguationData":[OSD([sQuery(id+"F1.wireOp",EDGE,"E6")])],"isStart":false});
            var Q17;
            Q17=makeQuery(id+"F3.opExtrude","CAP_EDGE",EDGE,{"disambiguationData":[OSD([sQuery(id+"F1.wireOp",EDGE,"E1")])],"isStart":false});
            var Q18;
            Q18=makeQuery(id+"F3.opExtrude","CAP_EDGE",EDGE,{"disambiguationData":[OSD([sQuery(id+"F1.wireOp",EDGE,"E19")])],"isStart":false});
            var Q19;
            Q19=makeQuery(id+"F3.opExtrude","CAP_EDGE",EDGE,{"disambiguationData":[OSD([sQuery(id+"F1.wireOp",EDGE,"E20")])],"isStart":false});
            var Q20;
            Q20=makeQuery(id+"F3.opExtrude","CAP_EDGE",EDGE,{"disambiguationData":[OSD([sQuery(id+"F1.wireOp",EDGE,"E22")])],"isStart":false});
            var Q21;
            Q21=makeQuery(id+"F3.opExtrude","CAP_EDGE",EDGE,{"disambiguationData":[OSD([sQuery(id+"F1.wireOp",EDGE,"E21")])],"isStart":false});
            var Q22;
            Q22=makeQuery(id+"F3.opExtrude","CAP_EDGE",EDGE,{"disambiguationData":[OSD([sQuery(id+"F1.wireOp",EDGE,"E23")])],"isStart":false});
            var Q23;
            Q23=makeQuery(id+"F3.opExtrude","CAP_EDGE",EDGE,{"disambiguationData":[OSD([sQuery(id+"F1.wireOp",EDGE,"E24")])],"isStart":false});
            var Q24;
            Q24=makeQuery(id+"F3.opExtrude","CAP_EDGE",EDGE,{"disambiguationData":[OSD([sQuery(id+"F0.wireOp",EDGE,"E0")])],"isStart":false});
            var Q25;
            Q25=makeQuery(id+"F3.opExtrude","CAP_EDGE",EDGE,{"disambiguationData":[OSD([sQuery(id+"F1.wireOp",EDGE,"E25")])],"isStart":false});
            var Q26;
            Q26=makeQuery(id+"F3.opExtrude","CAP_EDGE",EDGE,{"disambiguationData":[OSD([sQuery(id+"F1.wireOp",EDGE,"E26")])],"isStart":false});
            var Q27;
            Q27=makeQuery(id+"F3.opExtrude","CAP_EDGE",EDGE,{"disambiguationData":[OSD([sQuery(id+"F1.wireOp",EDGE,"E27")])],"isStart":false});
            var Q28;
            Q28=makeQuery(id+"F3.opExtrude","CAP_EDGE",EDGE,{"disambiguationData":[OSD([sQuery(id+"F1.wireOp",EDGE,"E28")])],"isStart":false});
            var Q29;
            Q29=makeQuery(id+"F3.opExtrude","CAP_EDGE",EDGE,{"disambiguationData":[OSD([sQuery(id+"F1.wireOp",EDGE,"E29")])],"isStart":false});
            var Q30;
            Q30=makeQuery(id+"F3.opExtrude","CAP_EDGE",EDGE,{"disambiguationData":[OSD([sQuery(id+"F1.wireOp",EDGE,"E30")])],"isStart":false});
            var Q31;
            Q31=makeQuery(id+"F3.opExtrude","CAP_EDGE",EDGE,{"disambiguationData":[OSD([sQuery(id+"F1.wireOp",EDGE,"E31")])],"isStart":false});
            var Q32;
            Q32=makeQuery(id+"F3.opExtrude","CAP_EDGE",EDGE,{"disambiguationData":[OSD([sQuery(id+"F1.wireOp",EDGE,"E32")])],"isStart":false});
            var Q33;
            Q33=makeQuery(id+"F3.opExtrude","CAP_EDGE",EDGE,{"disambiguationData":[OSD([sQuery(id+"F1.wireOp",EDGE,"E33")])],"isStart":false});
            var Q34;
            Q34=makeQuery(id+"F3.opExtrude","CAP_EDGE",EDGE,{"disambiguationData":[OSD([sQuery(id+"F1.wireOp",EDGE,"E34")])],"isStart":false});
            var Q35;
            Q35=makeQuery(id+"F3.opExtrude","CAP_EDGE",EDGE,{"disambiguationData":[OSD([sQuery(id+"F1.wireOp",EDGE,"E35")])],"isStart":false});
            var Q36;
            Q36=makeQuery(id+"F3.opExtrude","CAP_EDGE",EDGE,{"disambiguationData":[OSD([sQuery(id+"F1.wireOp",EDGE,"E38")])],"isStart":false});
            var Q37;
            Q37=makeQuery(id+"F3.opExtrude","CAP_EDGE",EDGE,{"disambiguationData":[OSD([sQuery(id+"F1.wireOp",EDGE,"E36")])],"isStart":false});
            var Q38;
            Q38=makeQuery(id+"F3.opExtrude","CAP_EDGE",EDGE,{"disambiguationData":[OSD([sQuery(id+"F1.wireOp",EDGE,"E37")])],"isStart":false});
            var Q39;
            Q39=makeQuery(id+"F3.opExtrude","CAP_EDGE",EDGE,{"disambiguationData":[OSD([sQuery(id+"F1.wireOp",EDGE,"E39")])],"isStart":false});
            var Q40;
            Q40=makeQuery(id+"F3.opExtrude","CAP_EDGE",EDGE,{"disambiguationData":[OSD([sQuery(id+"F1.wireOp",EDGE,"E43")])],"isStart":false});
            var Q41;
            Q41=makeQuery(id+"F3.opExtrude","CAP_EDGE",EDGE,{"disambiguationData":[OSD([sQuery(id+"F1.wireOp",EDGE,"E40")])],"isStart":false});
            var Q42;
            Q42=makeQuery(id+"F3.opExtrude","CAP_EDGE",EDGE,{"disambiguationData":[OSD([sQuery(id+"F1.wireOp",EDGE,"E42")])],"isStart":false});
            var Q43;
            Q43=makeQuery(id+"F3.opExtrude","CAP_EDGE",EDGE,{"disambiguationData":[OSD([sQuery(id+"F1.wireOp",EDGE,"E41")])],"isStart":false});
            var Q44;
            Q44=makeQuery(id+"F3.opExtrude","CAP_EDGE",EDGE,{"disambiguationData":[OSD([sQuery(id+"F1.wireOp",EDGE,"E44")])],"isStart":false});
            var Q45;
            Q45=makeQuery(id+"F3.opExtrude","CAP_EDGE",EDGE,{"disambiguationData":[OSD([sQuery(id+"F1.wireOp",EDGE,"E45")])],"isStart":false});
            var Q46;
            Q46=makeQuery(id+"F3.opExtrude","CAP_EDGE",EDGE,{"disambiguationData":[OSD([sQuery(id+"F1.wireOp",EDGE,"E46")])],"isStart":false});
            var Q47;
            Q47=makeQuery(id+"F3.opExtrude","CAP_EDGE",EDGE,{"disambiguationData":[OSD([sQuery(id+"F1.wireOp",EDGE,"E47")])],"isStart":false});
            var Q48;
            Q48=makeQuery(id+"F3.opExtrude","CAP_EDGE",EDGE,{"disambiguationData":[OSD([sQuery(id+"F1.wireOp",EDGE,"E48")])],"isStart":false});
            var Q49;
            Q49=makeQuery(id+"F3.opExtrude","CAP_EDGE",EDGE,{"disambiguationData":[OSD([sQuery(id+"F1.wireOp",EDGE,"E49")])],"isStart":false});
            var Q50;
            Q50=makeQuery(id+"F3.opExtrude","CAP_EDGE",EDGE,{"disambiguationData":[OSD([sQuery(id+"F1.wireOp",EDGE,"E50")])],"isStart":false});
            var Q51;
            Q51=makeQuery(id+"F3.opExtrude","CAP_EDGE",EDGE,{"disambiguationData":[OSD([sQuery(id+"F1.wireOp",EDGE,"E51")])],"isStart":false});
            var Q52;
            Q52=makeQuery(id+"F3.opExtrude","CAP_EDGE",EDGE,{"disambiguationData":[OSD([sQuery(id+"F1.wireOp",EDGE,"E52")])],"isStart":false});
            var Q53;
            Q53=makeQuery(id+"F3.opExtrude","CAP_EDGE",EDGE,{"disambiguationData":[OSD([sQuery(id+"F1.wireOp",EDGE,"E53")])],"isStart":false});
            var Q54;
            Q54=makeQuery(id+"F3.opExtrude","CAP_EDGE",EDGE,{"disambiguationData":[OSD([sQuery(id+"F1.wireOp",EDGE,"E54")])],"isStart":false});
            var Q55;
            Q55=makeQuery(id+"F3.opExtrude","CAP_EDGE",EDGE,{"disambiguationData":[OSD([sQuery(id+"F1.wireOp",EDGE,"E58")])],"isStart":false});
            var Q56;
            Q56=makeQuery(id+"F3.opExtrude","CAP_EDGE",EDGE,{"disambiguationData":[OSD([sQuery(id+"F1.wireOp",EDGE,"E57")])],"isStart":false});
            var Q57;
            Q57=makeQuery(id+"F3.opExtrude","CAP_EDGE",EDGE,{"disambiguationData":[OSD([sQuery(id+"F1.wireOp",EDGE,"E56")])],"isStart":false});
            var Q58;
            Q58=makeQuery(id+"F3.opExtrude","CAP_EDGE",EDGE,{"disambiguationData":[OSD([sQuery(id+"F1.wireOp",EDGE,"E55")])],"isStart":false});
            var Q59;
            Q59=makeQuery(id+"F3.opExtrude","CAP_EDGE",EDGE,{"disambiguationData":[OSD([sQuery(id+"F1.wireOp",EDGE,"E59")])],"isStart":false});
            var Q60;
            Q60=makeQuery(id+"F3.opExtrude","CAP_EDGE",EDGE,{"disambiguationData":[OSD([sQuery(id+"F1.wireOp",EDGE,"E61")])],"isStart":false});
            var Q61;
            Q61=makeQuery(id+"F3.opExtrude","CAP_EDGE",EDGE,{"disambiguationData":[OSD([sQuery(id+"F1.wireOp",EDGE,"E60")])],"isStart":false});
            var Q62;
            Q62=makeQuery(id+"F3.opExtrude","CAP_EDGE",EDGE,{"disambiguationData":[OSD([sQuery(id+"F1.wireOp",EDGE,"E62")])],"isStart":false});
            var Q63;
            Q63=makeQuery(id+"F3.opExtrude","CAP_EDGE",EDGE,{"disambiguationData":[OSD([sQuery(id+"F1.wireOp",EDGE,"E63")])],"isStart":false});
            var Q64;
            Q64=makeQuery(id+"F3.opExtrude","CAP_EDGE",EDGE,{"disambiguationData":[OSD([sQuery(id+"F1.wireOp",EDGE,"E64")])],"isStart":false});
            var Q65;
            Q65=makeQuery(id+"F3.opExtrude","CAP_EDGE",EDGE,{"disambiguationData":[OSD([sQuery(id+"F1.wireOp",EDGE,"E65")])],"isStart":false});
            var Q66;
            Q66=makeQuery(id+"F3.opExtrude","CAP_EDGE",EDGE,{"disambiguationData":[OSD([sQuery(id+"F1.wireOp",EDGE,"E68")])],"isStart":false});
            var Q67;
            Q67=makeQuery(id+"F3.opExtrude","CAP_EDGE",EDGE,{"disambiguationData":[OSD([sQuery(id+"F1.wireOp",EDGE,"E67")])],"isStart":false});
            var Q68;
            Q68=makeQuery(id+"F3.opExtrude","CAP_EDGE",EDGE,{"disambiguationData":[OSD([sQuery(id+"F1.wireOp",EDGE,"E66")])],"isStart":false});
            var Q69;
            Q69=makeQuery(id+"F3.opExtrude","CAP_EDGE",EDGE,{"disambiguationData":[OSD([sQuery(id+"F1.wireOp",EDGE,"E69")])],"isStart":false});
            var Q70;
            Q70=makeQuery(id+"F3.opExtrude","CAP_EDGE",EDGE,{"disambiguationData":[OSD([sQuery(id+"F1.wireOp",EDGE,"E70")])],"isStart":false});
            var Q71;
            Q71=makeQuery(id+"F3.opExtrude","CAP_EDGE",EDGE,{"disambiguationData":[OSD([sQuery(id+"F1.wireOp",EDGE,"E71")])],"isStart":false});
            var Q72;
            Q72=makeQuery(id+"F3.opExtrude","CAP_EDGE",EDGE,{"disambiguationData":[OSD([sQuery(id+"F1.wireOp",EDGE,"E72")])],"isStart":false});
            var Q73;
            Q73=makeQuery(id+"F3.opExtrude","CAP_EDGE",EDGE,{"disambiguationData":[OSD([sQuery(id+"F1.wireOp",EDGE,"E73")])],"isStart":false});
            var Q74;
            Q74=makeQuery(id+"F3.opExtrude","CAP_EDGE",EDGE,{"disambiguationData":[OSD([sQuery(id+"F1.wireOp",EDGE,"E74")])],"isStart":false});
            var Q75;
            Q75=makeQuery(id+"F3.opExtrude","CAP_EDGE",EDGE,{"disambiguationData":[OSD([sQuery(id+"F1.wireOp",EDGE,"E76")])],"isStart":false});
            var Q76;
            Q76=makeQuery(id+"F3.opExtrude","CAP_EDGE",EDGE,{"disambiguationData":[OSD([sQuery(id+"F1.wireOp",EDGE,"E75")])],"isStart":false});
            var Q77;
            Q77=makeQuery(id+"F3.opExtrude","CAP_EDGE",EDGE,{"disambiguationData":[OSD([sQuery(id+"F1.wireOp",EDGE,"E77")])],"isStart":false});
            var Q78;
            Q78=makeQuery(id+"F3.opExtrude","CAP_EDGE",EDGE,{"disambiguationData":[OSD([sQuery(id+"F1.wireOp",EDGE,"E78")])],"isStart":false});
            var Q79;
            Q79=makeQuery(id+"F3.opExtrude","CAP_EDGE",EDGE,{"disambiguationData":[OSD([sQuery(id+"F1.wireOp",EDGE,"E79")])],"isStart":false});
            var Q80;
            Q80=makeQuery(id+"F3.opExtrude","CAP_EDGE",EDGE,{"disambiguationData":[OSD([sQuery(id+"F1.wireOp",EDGE,"E80")])],"isStart":false});
            var Q81;
            Q81=makeQuery(id+"F3.opExtrude","CAP_EDGE",EDGE,{"disambiguationData":[OSD([sQuery(id+"F1.wireOp",EDGE,"E81")])],"isStart":false});
            var Q82;
            Q82=makeQuery(id+"F3.opExtrude","CAP_EDGE",EDGE,{"disambiguationData":[OSD([sQuery(id+"F1.wireOp",EDGE,"E82")])],"isStart":false});
            var Q83;
            Q83=makeQuery(id+"F3.opExtrude","CAP_EDGE",EDGE,{"disambiguationData":[OSD([sQuery(id+"F1.wireOp",EDGE,"E83")])],"isStart":false});
            var Q84;
            Q84=makeQuery(id+"F3.opExtrude","CAP_EDGE",EDGE,{"disambiguationData":[OSD([sQuery(id+"F1.wireOp",EDGE,"E85")])],"isStart":false});
            var Q85;
            Q85=makeQuery(id+"F3.opExtrude","CAP_EDGE",EDGE,{"disambiguationData":[OSD([sQuery(id+"F1.wireOp",EDGE,"E84")])],"isStart":false});
            var Q86;
            Q86=makeQuery(id+"F3.opExtrude","CAP_EDGE",EDGE,{"disambiguationData":[OSD([sQuery(id+"F1.wireOp",EDGE,"E86")])],"isStart":false});
            var Q87;
            Q87=makeQuery(id+"F3.opExtrude","CAP_EDGE",EDGE,{"disambiguationData":[OSD([sQuery(id+"F1.wireOp",EDGE,"E87")])],"isStart":false});
            var Q88;
            Q88=makeQuery(id+"F3.opExtrude","CAP_EDGE",EDGE,{"disambiguationData":[OSD([sQuery(id+"F1.wireOp",EDGE,"E88")])],"isStart":false});
            var Q89;
            Q89=makeQuery(id+"F3.opExtrude","CAP_EDGE",EDGE,{"disambiguationData":[OSD([sQuery(id+"F1.wireOp",EDGE,"E89")])],"isStart":false});
            var Q90;
            Q90=makeQuery(id+"F3.opExtrude","CAP_FACE",FACE,{"disambiguationData":[OSD([sQuery(id+"F1.wireOp",EDGE,"E90")])],"isStart":false});
            var Q91;
            Q91=makeQuery(id+"F3.opExtrude","CAP_EDGE",EDGE,{"disambiguationData":[OSD([sQuery(id+"F1.wireOp",EDGE,"E90")])],"isStart":false});
            var Q92;
            Q92=makeQuery(id+"F3.opExtrude","CAP_EDGE",EDGE,{"disambiguationData":[OSD([sQuery(id+"F1.wireOp",EDGE,"E91")])],"isStart":false});
            var Q93;
            Q93=makeQuery(id+"F3.opExtrude","CAP_EDGE",EDGE,{"disambiguationData":[OSD([sQuery(id+"F1.wireOp",EDGE,"E92")])],"isStart":false});
            var Q94;
            Q94=makeQuery(id+"F3.opExtrude","CAP_EDGE",EDGE,{"disambiguationData":[OSD([sQuery(id+"F1.wireOp",EDGE,"E93")])],"isStart":false});
            var Q95;
            Q95=makeQuery(id+"F3.opExtrude","CAP_EDGE",EDGE,{"disambiguationData":[OSD([sQuery(id+"F1.wireOp",EDGE,"E95")])],"isStart":false});
            var Q96;
            Q96=makeQuery(id+"F3.opExtrude","CAP_EDGE",EDGE,{"disambiguationData":[OSD([sQuery(id+"F1.wireOp",EDGE,"E96")])],"isStart":false});
            var Q97;
            Q97=makeQuery(id+"F3.opExtrude","CAP_EDGE",EDGE,{"disambiguationData":[OSD([sQuery(id+"F1.wireOp",EDGE,"E100")])],"isStart":false});
            var Q98;
            Q98=makeQuery(id+"F3.opExtrude","CAP_EDGE",EDGE,{"disambiguationData":[OSD([sQuery(id+"F1.wireOp",EDGE,"E103")])],"isStart":false});
            var Q99;
            Q99=makeQuery(id+"F3.opExtrude","CAP_EDGE",EDGE,{"disambiguationData":[OSD([sQuery(id+"F1.wireOp",EDGE,"E99")])],"isStart":false});
            var Q100;
            Q100=makeQuery(id+"F3.opExtrude","CAP_EDGE",EDGE,{"disambiguationData":[OSD([sQuery(id+"F1.wireOp",EDGE,"E102")])],"isStart":false});
            var Q101;
            Q101=makeQuery(id+"F3.opExtrude","CAP_EDGE",EDGE,{"disambiguationData":[OSD([sQuery(id+"F1.wireOp",EDGE,"E98")])],"isStart":false});
            var Q102;
            Q102=makeQuery(id+"F3.opExtrude","CAP_EDGE",EDGE,{"disambiguationData":[OSD([sQuery(id+"F1.wireOp",EDGE,"E97")])],"isStart":false});
            var Q103;
            Q103=makeQuery(id+"F3.opExtrude","CAP_EDGE",EDGE,{"disambiguationData":[OSD([sQuery(id+"F1.wireOp",EDGE,"E94")])],"isStart":false});
            var Q104;
            Q104=makeQuery(id+"F3.opExtrude","CAP_EDGE",EDGE,{"disambiguationData":[OSD([sQuery(id+"F1.wireOp",EDGE,"E105")])],"isStart":false});
            var Q105;
            Q105=makeQuery(id+"F3.opExtrude","CAP_EDGE",EDGE,{"disambiguationData":[OSD([sQuery(id+"F1.wireOp",EDGE,"E106")])],"isStart":false});
            var Q106;
            Q106=makeQuery(id+"F3.opExtrude","CAP_EDGE",EDGE,{"disambiguationData":[OSD([sQuery(id+"F1.wireOp",EDGE,"E107")])],"isStart":false});
            var Q107;
            Q107=makeQuery(id+"F3.opExtrude","CAP_EDGE",EDGE,{"disambiguationData":[OSD([sQuery(id+"F1.wireOp",EDGE,"E108")])],"isStart":false});
            var Q108;
            Q108=makeQuery(id+"F3.opExtrude","CAP_EDGE",EDGE,{"disambiguationData":[OSD([sQuery(id+"F1.wireOp",EDGE,"E109")])],"isStart":false});
            var Q109;
            Q109=makeQuery(id+"F3.opExtrude","CAP_EDGE",EDGE,{"disambiguationData":[OSD([sQuery(id+"F1.wireOp",EDGE,"E104")])],"isStart":false});
            var Q110;
            Q110=makeQuery(id+"F3.opExtrude","CAP_EDGE",EDGE,{"disambiguationData":[OSD([sQuery(id+"F1.wireOp",EDGE,"E101")])],"isStart":false});
            fillet(context, id + "F4", {"entities" : qUnion([Q0, Q1, Q2, Q3, Q4, Q5, Q6, Q7, Q8, Q9, Q10, Q11, Q12, Q13, Q14, Q15, Q16, Q17, Q18, Q19, Q20, Q21, Q22, Q23, Q24, Q25, Q26, Q27, Q28, Q29, Q30, Q31, Q32, Q33, Q34, Q35, Q36, Q37, Q38, Q39, Q40, Q41, Q42, Q43, Q44, Q45, Q46, Q47, Q48, Q49, Q50, Q51, Q52, Q53, Q54, Q55, Q56, Q57, Q58, Q59, Q60, Q61, Q62, Q63, Q64, Q65, Q66, Q67, Q68, Q69, Q70, Q71, Q72, Q73, Q74, Q75, Q76, Q77, Q78, Q79, Q80, Q81, Q82, Q83, Q84, Q85, Q86, Q87, Q88, Q89, Q90, Q91, Q92, Q93, Q94, Q95, Q96, Q97, Q98, Q99, Q100, Q101, Q102, Q103, Q104, Q105, Q106, Q107, Q108, Q109, Q110]), "radius" : .6 * mm, "tangentPropagation" : true, "rho" : .3, "crossSection" : FilletCrossSection.CONIC, "allowEdgeOverflow" : false});
        }
        {
            var Q0;
            {var subQ1=sQuery(id+"F2.wireOp",EDGE,"wk7LG9wq-JaKf-7Txt-Pqvq-ZvWdc8VFdTcg.bottom");Q0=makeQuery(id+"F2.imprint","IMPRINT",FACE,{"disambiguationData":[TD([[makeQuery(id+"F2.imprint","IMPRINT",EDGE,{"derivedFrom":subQ1}),-1.0]])]});}
            var Q1;
            Q1=makeQuery(id+"F1.imprint","IMPRINT",FACE,{"disambiguationData":[TD([[makeQuery(id+"F1.imprint","IMPRINT",EDGE,{"derivedFrom":sQuery(id+"F1.wireOp",EDGE,"E1")}),-1.0]])]});
            var Q2;
            {var subQ0=sQuery(id+"F1.wireOp",EDGE,"E114");Q2=makeQuery(id+"F1.imprint","IMPRINT",FACE,{"disambiguationData":[TD([[makeQuery(id+"F1.imprint","IMPRINT",EDGE,{"derivedFrom":subQ0}),-1.0]])]});}
            extrude(context, id + "F5", {"entities" : qUnion([Q0, Q1, Q2]), "oppositeDirection" : true, "depth" : 1.02 * mm});
        }
        {
            var Q0;
            Q0=makeQuery(id+"F3.opExtrude","SWEPT_BODY",BODY,{"disambiguationData":[OSD([sQuery(id+"F0.wireOp",EDGE,"E0")])]});
            deleteBodies(context, id + "F6", {"entities" : qUnion([Q0])});
        }
    });
